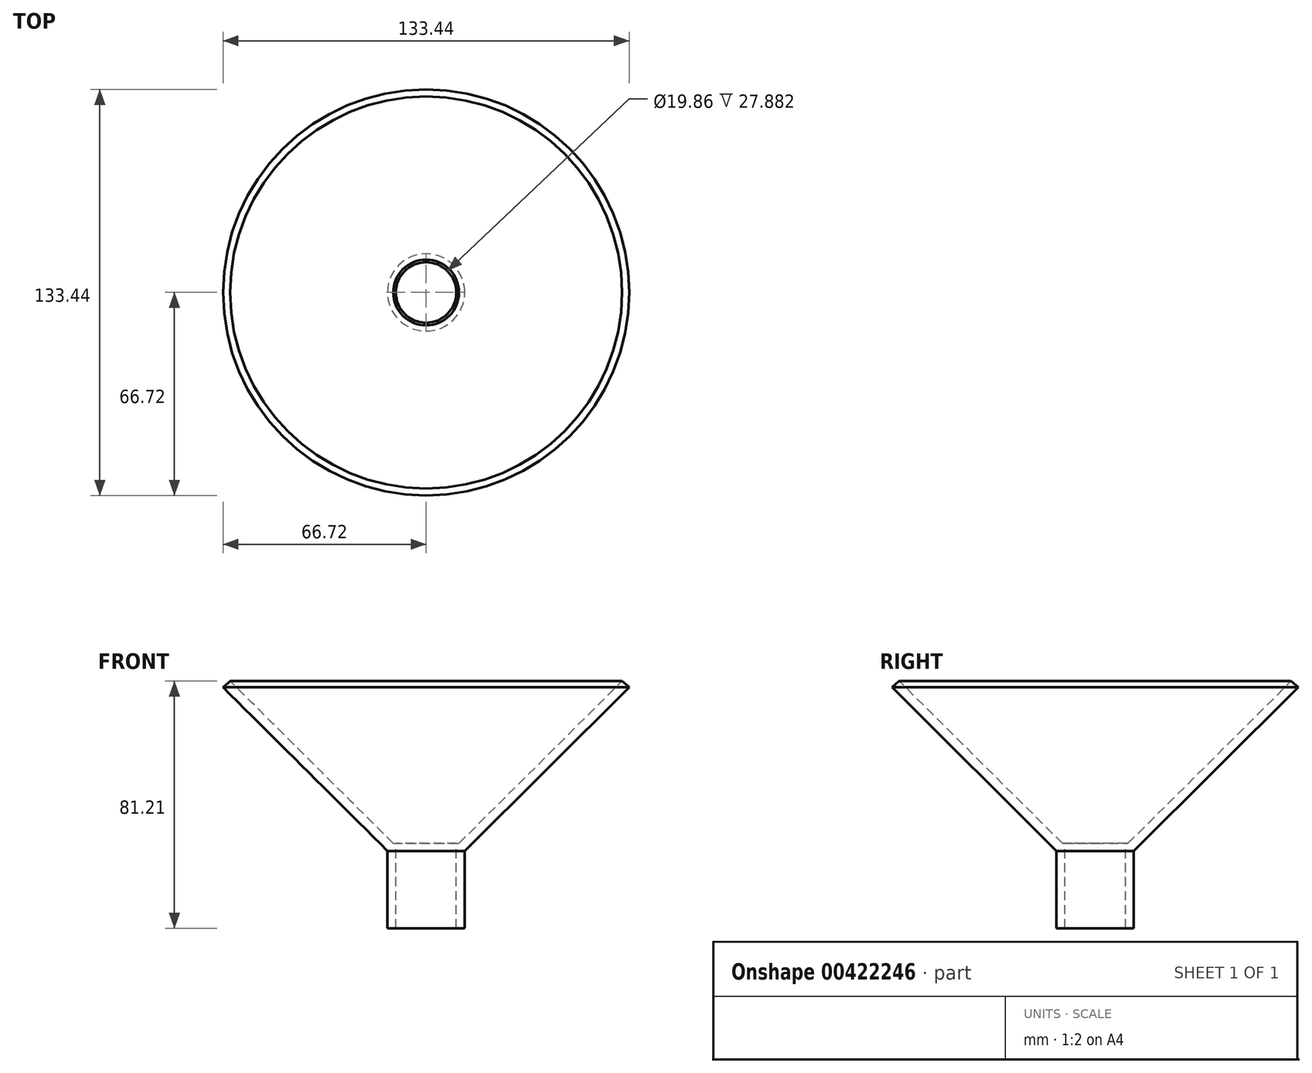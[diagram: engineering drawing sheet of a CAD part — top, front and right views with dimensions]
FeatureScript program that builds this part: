
annotation { "Feature Type Name" : "Feature", "Feature Type Description" : "" }
export const myFeature = defineFeature(function(context is Context, id is Id, definition is map)
    precondition{}
    {
        {
            var Q0;
            Q0=qCreatedBy(makeId("Front.planeOp"),FACE);
            var sketch = newSketch(context, id + "F0", { "sketchPlane" : qUnion([Q0])});
            skLineSegment(sketch, "E0", {"start": v(0, 0) * mm, "end": v(54.02, 53.75) * mm});
            skLineSegment(sketch, "E1", {"start": v(0, 0) * mm, "end": v(0, -25.4) * mm});
            skLineSegment(sketch, "E2", {"start": v(0, -25.4) * mm, "end": v(-12.7, -25.4) * mm});
            skLineSegment(sketch, "E3", {"start": v(-12.7, -25.4) * mm, "end": v(-12.7, 2.48) * mm});
            skLineSegment(sketch, "E4", {"start": v(-12.7, 2.48) * mm, "end": v(-1.9, 2.48) * mm});
            skLineSegment(sketch, "E5", {"start": v(-1.9, 2.48) * mm, "end": v(51.7, 55.81) * mm});
            skLineSegment(sketch, "E6", {"start": v(51.7, 55.81) * mm, "end": v(54.02, 53.75) * mm});
            skSolve(sketch);
        }
        {
            var Q0;
            Q0 = qSketchRegion(id + "F0", true);
            var Q1;
            Q1=sQuery(id+"F0.wireOp",EDGE,"E3");
            revolve(context, id + "F1", {"entities" : qUnion([Q0]), "axis" : qUnion([Q1]), "revolveType" : RevolveType.FULL});
        }
        {
            var Q0;
            Q0=makeQuery(id+"F1.opRevolve","SWEPT_FACE",FACE,{"disambiguationData":[OSD([sQuery(id+"F0.wireOp",EDGE,"E4")])]});
            var sketch = newSketch(context, id + "F2", { "sketchPlane" : qUnion([Q0])});
            skCircle(sketch, "E7", {"center": v(-12.7, 0) * mm, "radius": 9.93 * mm});
            skSolve(sketch);
        }
        {
            var Q0;
            Q0=makeQuery(id+"F2.imprint","IMPRINT",FACE,{"disambiguationData":[TD([[makeQuery(id+"F2.imprint","IMPRINT",EDGE,{"derivedFrom":sQuery(id+"F2.wireOp",EDGE,"E7")}),1.0]])]});
            extrude(context, id + "F3", {"entities" : qUnion([Q0]), "operationType" : NewBodyOperationType.REMOVE, "oppositeDirection" : true, "depth" : 50.8 * mm, "offsetDistance" : 25.4 * mm});
        }
    });
